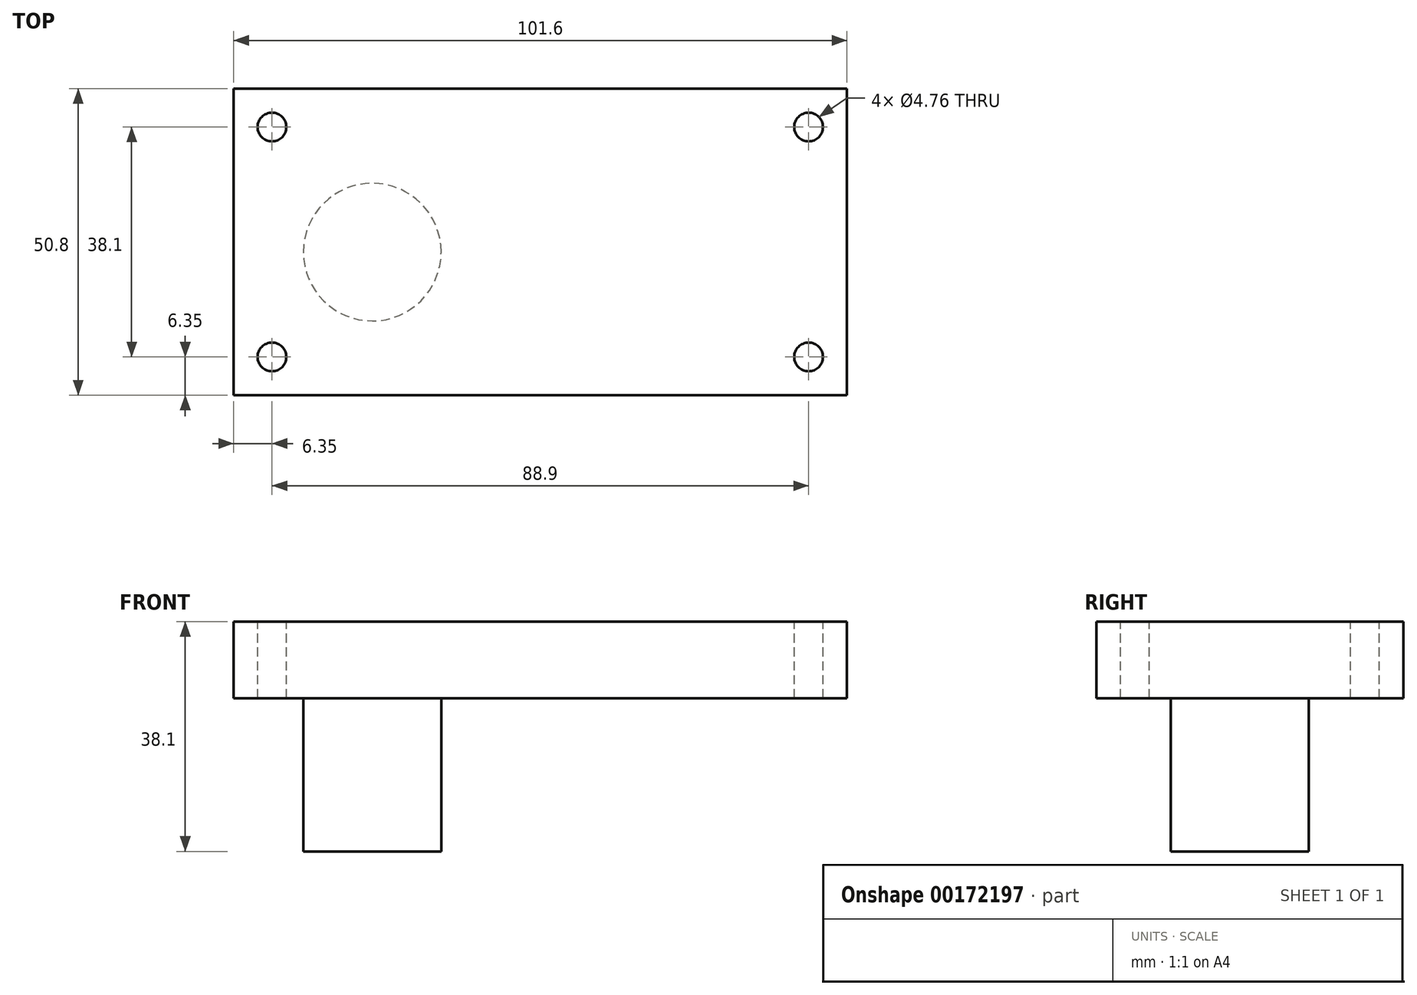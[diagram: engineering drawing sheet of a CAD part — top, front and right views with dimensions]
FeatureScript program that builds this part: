
annotation { "Feature Type Name" : "Feature", "Feature Type Description" : "" }
export const myFeature = defineFeature(function(context is Context, id is Id, definition is map)
    precondition{}
    {
        {
            var Q0;
            Q0=qCreatedBy(makeId("Top.planeOp"),FACE);
            var sketch = newSketch(context, id + "F0", { "sketchPlane" : qUnion([Q0])});
            skLineSegment(sketch, "E0.bottom", {"start": v(0, 0) * mm, "end": v(101.6, 0) * mm});
            skLineSegment(sketch, "E0.top", {"start": v(0, -50.8) * mm, "end": v(101.6, -50.8) * mm});
            skLineSegment(sketch, "E0.left", {"start": v(0, 0) * mm, "end": v(0, -50.8) * mm});
            skLineSegment(sketch, "E0.right", {"start": v(101.6, 0) * mm, "end": v(101.6, -50.8) * mm});
            skCircle(sketch, "E1", {"center": v(6.35, -44.45) * mm, "radius": 2.38 * mm});
            skCircle(sketch, "E2", {"center": v(6.35, -6.35) * mm, "radius": 2.38 * mm});
            skCircle(sketch, "E3", {"center": v(95.25, -44.45) * mm, "radius": 2.38 * mm});
            skCircle(sketch, "E4", {"center": v(95.25, -6.35) * mm, "radius": 2.38 * mm});
            skSolve(sketch);
        }
        {
            var Q0;
            Q0=makeQuery(id+"F0.imprint","IMPRINT",FACE,{"disambiguationData":[TD([[makeQuery(id+"F0.imprint","IMPRINT",EDGE,{"derivedFrom":sQuery(id+"F0.wireOp",EDGE,"E0.bottom")}),-1.0]])]});
            extrude(context, id + "F1", {"entities" : qUnion([Q0]), "oppositeDirection" : true, "depth" : 12.7 * mm});
        }
        {
            var Q0;
            Q0=makeQuery(id+"F1.opExtrude","CAP_FACE",FACE,{"disambiguationData":[OSD([sQuery(id+"F0.wireOp",EDGE,"E0.bottom"),sQuery(id+"F0.wireOp",EDGE,"E0.top"),sQuery(id+"F0.wireOp",EDGE,"E0.left"),sQuery(id+"F0.wireOp",EDGE,"E0.right"),sQuery(id+"F0.wireOp",EDGE,"E1"),sQuery(id+"F0.wireOp",EDGE,"E2"),sQuery(id+"F0.wireOp",EDGE,"E3"),sQuery(id+"F0.wireOp",EDGE,"E4")])],"isStart":false});
            var sketch = newSketch(context, id + "F2", { "sketchPlane" : qUnion([Q0])});
            skCircle(sketch, "E5", {"center": v(22.97, 27.08) * mm, "radius": 11.4 * mm});
            skSolve(sketch);
        }
        {
            var Q0;
            Q0 = qSketchRegion(id + "F2", true);
            extrude(context, id + "F3", {"entities" : qUnion([Q0]), "operationType" : NewBodyOperationType.ADD, "depth" : 25.4 * mm});
        }
    });
